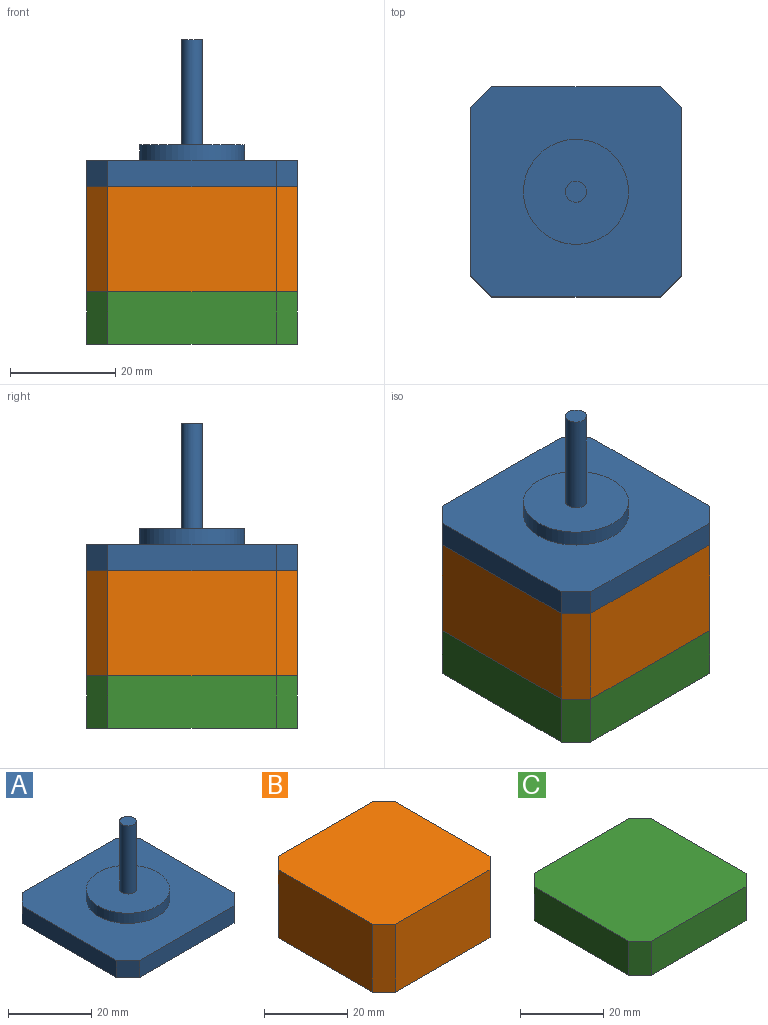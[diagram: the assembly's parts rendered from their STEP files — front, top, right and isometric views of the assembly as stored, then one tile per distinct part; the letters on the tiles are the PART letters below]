
ASSEMBLY  parts=3 mates=2
PART A: 14 faces, bbox 40x40x28 mm
  f0: plane 32x5mm, normal (0,1,0), area 160mm2, adj f4,f5,f10,f11
  f1: plane 32x5mm, normal (-1,0,0), area 160mm2, adj f4,f5,f10,f13
  f2: plane 32x5mm, normal (0,-1,0), area 160mm2, adj f4,f5,f12,f13
  f3: plane 32x5mm, normal (1,0,0), area 160mm2, adj f4,f5,f11,f12
  f4: plane 40x40mm, normal (0,0,1), area 1253.8mm2, adj f0,f1,f2,f3,f6,f10,f11,f12
  f5: plane 40x40mm, normal (0,0,-1), area 1568mm2, adj f0,f1,f2,f3,f10,f11,f12,f13
  f6: cylinder r=10mm len=20mm, axis (0,0,-1), area 188.5mm2, adj f4,f7
  f7: plane 20x20mm, normal (0,0,1), area 301.6mm2, adj f6,f8
  f8: cylinder r=2mm len=20mm, axis (0,0,-1), area 251.3mm2, adj f7,f9
  f9: plane 4x4mm, normal (0,0,1), area 12.6mm2, adj f8
  f10: plane 5x4mm, normal (-0.71,0.71,0), area 28.3mm2, adj f0,f1,f4,f5
  f11: plane 5x4mm, normal (0.71,0.71,0), area 28.3mm2, adj f0,f3,f4,f5
  f12: plane 5x4mm, normal (0.71,-0.71,0), area 28.3mm2, adj f2,f3,f4,f5
  f13: plane 5x4mm, normal (-0.71,-0.71,0), area 28.3mm2, adj f1,f2,f4,f5
PART B: 10 faces, bbox 40x40x20 mm
  f0: plane 32x20mm, normal (0,1,0), area 640mm2, adj f4,f5,f6,f8
  f1: plane 32x20mm, normal (-1,0,0), area 640mm2, adj f4,f5,f8,f9
  f2: plane 32x20mm, normal (0,-1,0), area 640mm2, adj f4,f5,f7,f9
  f3: plane 32x20mm, normal (1,0,0), area 640mm2, adj f4,f5,f6,f7
  f4: plane 40x40mm, normal (0,0,1), area 1568mm2, adj f0,f1,f2,f3,f6,f7,f8,f9
  f5: plane 40x40mm, normal (0,0,-1), area 1568mm2, adj f0,f1,f2,f3,f6,f7,f8,f9
  f6: plane 20x4mm, normal (0.71,0.71,0), area 113.1mm2, adj f0,f3,f4,f5
  f7: plane 20x4mm, normal (0.71,-0.71,0), area 113.1mm2, adj f2,f3,f4,f5
  f8: plane 20x4mm, normal (-0.71,0.71,0), area 113.1mm2, adj f0,f1,f4,f5
  f9: plane 20x4mm, normal (-0.71,-0.71,0), area 113.1mm2, adj f1,f2,f4,f5
PART C: 10 faces, bbox 40x40x10 mm
  f0: plane 32x10mm, normal (0,1,0), area 320mm2, adj f4,f5,f6,f8
  f1: plane 32x10mm, normal (-1,0,0), area 320mm2, adj f4,f5,f8,f9
  f2: plane 32x10mm, normal (0,-1,0), area 320mm2, adj f4,f5,f7,f9
  f3: plane 32x10mm, normal (1,0,0), area 320mm2, adj f4,f5,f6,f7
  f4: plane 40x40mm, normal (0,0,1), area 1568mm2, adj f0,f1,f2,f3,f6,f7,f8,f9
  f5: plane 40x40mm, normal (0,0,-1), area 1568mm2, adj f0,f1,f2,f3,f6,f7,f8,f9
  f6: plane 10x4mm, normal (0.71,0.71,0), area 56.6mm2, adj f0,f3,f4,f5
  f7: plane 10x4mm, normal (0.71,-0.71,0), area 56.6mm2, adj f2,f3,f4,f5
  f8: plane 10x4mm, normal (-0.71,0.71,0), area 56.6mm2, adj f0,f1,f4,f5
  f9: plane 10x4mm, normal (-0.71,-0.71,0), area 56.6mm2, adj f1,f2,f4,f5
PLACE A t=(0,0,30)mm
PLACE B t=(0,0,10)mm
PLACE C at identity
MATE fastened B.f5 <-> C.f4  axis (0,0,-1) through (0,0,10)mm
MATE fastened A.f8 <-> B.f4  axis (0,0,-1) through (0,0,30)mm
